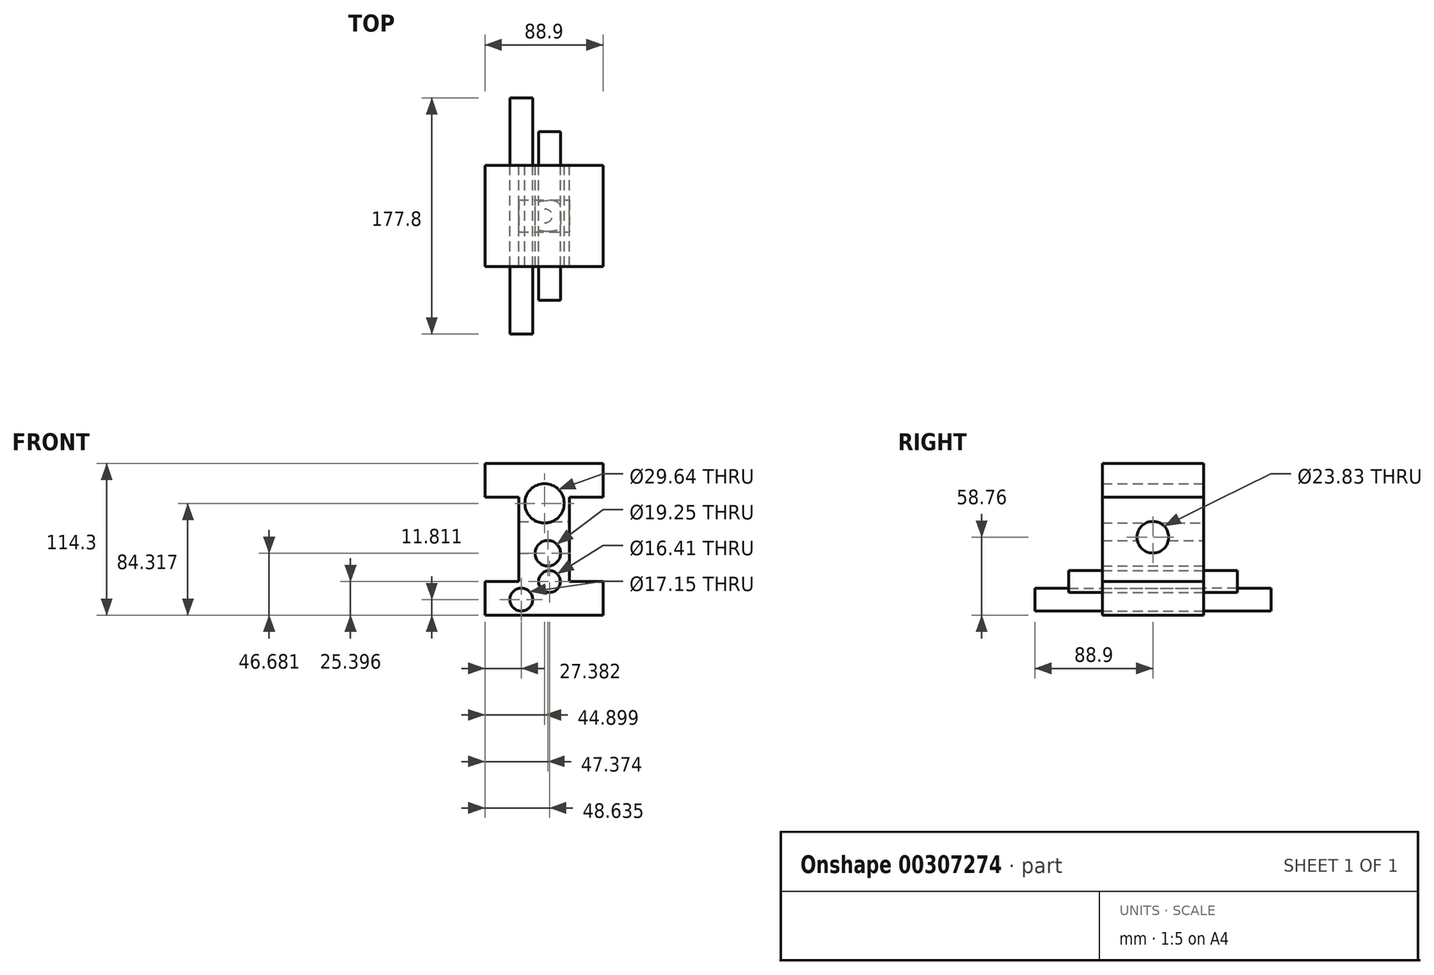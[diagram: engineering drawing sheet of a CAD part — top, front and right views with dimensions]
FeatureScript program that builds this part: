
annotation { "Feature Type Name" : "Feature", "Feature Type Description" : "" }
export const myFeature = defineFeature(function(context is Context, id is Id, definition is map)
    precondition{}
    {
        {
            var Q0;
            Q0=qCreatedBy(makeId("Front.planeOp"),FACE);
            var sketch = newSketch(context, id + "F0", { "sketchPlane" : qUnion([Q0])});
            skLineSegment(sketch, "E0", {"start": v(-38.05, -58.76) * mm, "end": v(50.85, -58.76) * mm});
            skLineSegment(sketch, "E1", {"start": v(50.85, -58.76) * mm, "end": v(50.85, -33.36) * mm});
            skLineSegment(sketch, "E2", {"start": v(50.85, -33.36) * mm, "end": v(25.45, -33.36) * mm});
            skLineSegment(sketch, "E3", {"start": v(25.45, -33.36) * mm, "end": v(25.45, 30.14) * mm});
            skLineSegment(sketch, "E4", {"start": v(25.45, 30.14) * mm, "end": v(50.85, 30.14) * mm});
            skLineSegment(sketch, "E5", {"start": v(50.85, 30.14) * mm, "end": v(50.85, 55.54) * mm});
            skLineSegment(sketch, "E6", {"start": v(50.85, 54.75) * mm, "end": v(50.85, 55.54) * mm});
            skLineSegment(sketch, "E7", {"start": v(-38.05, 55.54) * mm, "end": v(50.85, 55.54) * mm});
            skLineSegment(sketch, "E8", {"start": v(-38.05, 55.54) * mm, "end": v(-38.05, 30.14) * mm});
            skLineSegment(sketch, "E9", {"start": v(-38.05, 30.14) * mm, "end": v(-12.65, 30.14) * mm});
            skPoint(sketch, "E9.endSnap0", {"position": v(38.15, 30.14) * mm});
            skLineSegment(sketch, "E10", {"start": v(-12.65, 30.14) * mm, "end": v(-12.65, -33.36) * mm});
            skLineSegment(sketch, "E11", {"start": v(-12.65, -33.36) * mm, "end": v(-38.05, -33.36) * mm});
            skLineSegment(sketch, "E12", {"start": v(-38.05, -33.36) * mm, "end": v(-38.05, -58.76) * mm});
            skCircle(sketch, "E13", {"center": v(6.85, 25.56) * mm, "radius": 14.82 * mm});
            skCircle(sketch, "E14", {"center": v(9.32, -12.08) * mm, "radius": 9.62 * mm});
            skCircle(sketch, "E15", {"center": v(10.58, -33.36) * mm, "radius": 8.2 * mm});
            skCircle(sketch, "E16", {"center": v(-10.67, -46.95) * mm, "radius": 8.57 * mm});
            skSolve(sketch);
        }
        {
            var Q0;
            Q0=makeQuery(id+"F0.imprint","IMPRINT",FACE,{"disambiguationData":[TD([[makeQuery(id+"F0.imprint","IMPRINT",EDGE,{"derivedFrom":sQuery(id+"F0.wireOp",EDGE,"E0")}),1.0]])]});
            extrude(context, id + "F1", {"entities" : qUnion([Q0]), "depth" : 76.2 * mm});
        }
        {
            var Q0;
            Q0=makeQuery(id+"F1.opExtrude","CAP_FACE",FACE,{"disambiguationData":[OSD([sQuery(id+"F0.wireOp",EDGE,"E0"),sQuery(id+"F0.wireOp",EDGE,"E1"),sQuery(id+"F0.wireOp",EDGE,"E2"),sQuery(id+"F0.wireOp",EDGE,"E3"),sQuery(id+"F0.wireOp",EDGE,"E4"),sQuery(id+"F0.wireOp",EDGE,"E5"),sQuery(id+"F0.wireOp",EDGE,"E6"),sQuery(id+"F0.wireOp",EDGE,"E7"),sQuery(id+"F0.wireOp",EDGE,"E8"),sQuery(id+"F0.wireOp",EDGE,"E9"),sQuery(id+"F0.wireOp",EDGE,"E10"),sQuery(id+"F0.wireOp",EDGE,"E11"),sQuery(id+"F0.wireOp",EDGE,"E12")])],"isStart":false});
            var sketch = newSketch(context, id + "F2", { "sketchPlane" : qUnion([Q0])});
            skCircle(sketch, "E17", {"center": v(5.4, 0) * mm, "radius": 20.04 * mm});
            skSolve(sketch);
        }
        {
            var Q0;
            Q0=makeQuery(id+"F1.opExtrude","SWEPT_FACE",FACE,{"disambiguationData":[OSD([sQuery(id+"F0.wireOp",EDGE,"E3")])]});
            var sketch = newSketch(context, id + "F3", { "sketchPlane" : qUnion([Q0])});
            skCircle(sketch, "E18", {"center": v(-38.1, 0) * mm, "radius": 11.92 * mm});
            skPoint(sketch, "E18.centerSnap0", {"position": v(-38.1, -33.36) * mm});
            skSolve(sketch);
        }
        {
            var Q0;
            Q0 = qSketchRegion(id + "F3", true);
            extrude(context, id + "F4", {"entities" : qUnion([Q0]), "operationType" : NewBodyOperationType.REMOVE, "endBound" : BoundingType.THROUGH_ALL, "oppositeDirection" : true, "depth" : 25.4 * mm});
        }
        {
            var Q0;
            Q0=makeQuery(id+"F0.imprint","IMPRINT",FACE,{"disambiguationData":[TD([[makeQuery(id+"F0.imprint","IMPRINT",EDGE,{"derivedFrom":sQuery(id+"F0.wireOp",EDGE,"E15")}),1.0]])]});
            extrude(context, id + "F5", {"entities" : qUnion([Q0]), "operationType" : NewBodyOperationType.ADD, "oppositeDirection" : true, "depth" : 25.4 * mm});
        }
        {
            var Q0;
            Q0=makeQuery(id+"F0.imprint","IMPRINT",FACE,{"disambiguationData":[TD([[makeQuery(id+"F0.imprint","IMPRINT",EDGE,{"derivedFrom":sQuery(id+"F0.wireOp",EDGE,"E16")}),1.0]])]});
            extrude(context, id + "F6", {"entities" : qUnion([Q0]), "operationType" : NewBodyOperationType.ADD, "oppositeDirection" : true, "depth" : 50.8 * mm});
        }
        {
            var Q0;
            Q0=makeQuery(id+"F2.imprint","IMPRINT",FACE,{"disambiguationData":[TD([[makeQuery(id+"F2.imprint","IMPRINT",EDGE,{"derivedFrom":makeQuery(id+"F1.opExtrude","CAP_EDGE",EDGE,{"disambiguationData":[OSD([sQuery(id+"F0.wireOp",EDGE,"E15")])],"isStart":false})}),1.0]])]});
            extrude(context, id + "F7", {"entities" : qUnion([Q0]), "depth" : 25.4 * mm});
        }
        {
            var Q0;
            Q0=makeQuery(id+"F0.imprint","IMPRINT",FACE,{"disambiguationData":[TD([[makeQuery(id+"F0.imprint","IMPRINT",EDGE,{"derivedFrom":sQuery(id+"F0.wireOp",EDGE,"E16")}),1.0]])]});
            extrude(context, id + "F8", {"entities" : qUnion([Q0]), "depth" : 127 * mm});
        }
    });
